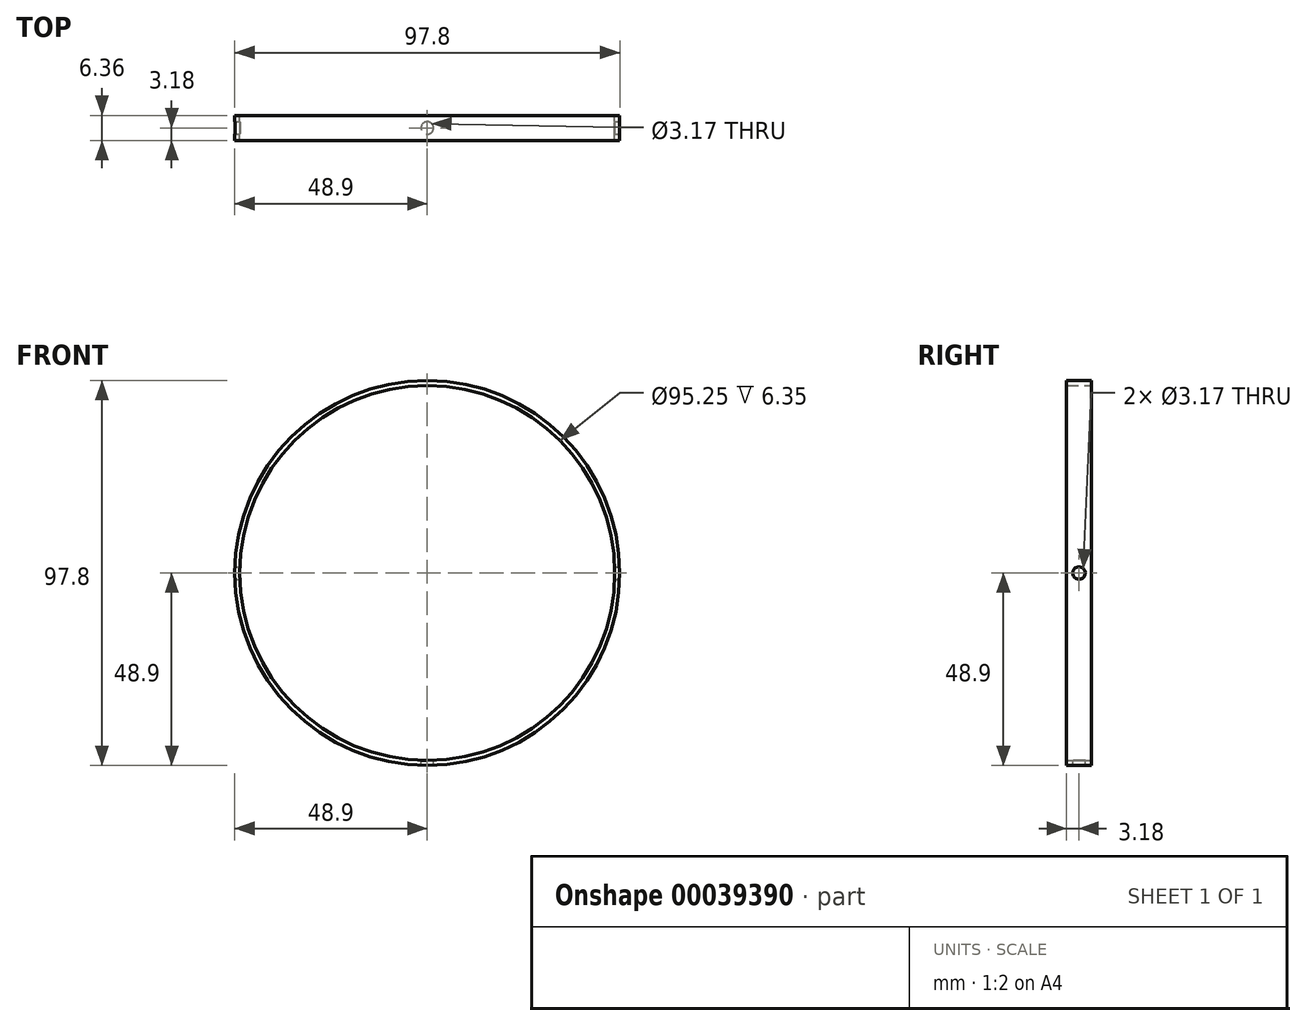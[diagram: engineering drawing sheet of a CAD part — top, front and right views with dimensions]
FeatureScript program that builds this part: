
annotation { "Feature Type Name" : "Feature", "Feature Type Description" : "" }
export const myFeature = defineFeature(function(context is Context, id is Id, definition is map)
    precondition{}
    {
        {
            var Q0;
            Q0=qCreatedBy(makeId("Front.planeOp"),FACE);
            var sketch = newSketch(context, id + "F0", { "sketchPlane" : qUnion([Q0])});
            skCircle(sketch, "E0", {"center": v(0, 0) * mm, "radius": 47.63 * mm});
            skCircle(sketch, "E1", {"center": v(0, 0) * mm, "radius": 48.9 * mm});
            skSolve(sketch);
        }
        {
            var Q0;
            Q0=makeQuery(id+"F0.imprint","IMPRINT",FACE,{"disambiguationData":[TD([[makeQuery(id+"F0.imprint","IMPRINT",EDGE,{"derivedFrom":sQuery(id+"F0.wireOp",EDGE,"E0")}),-1.0]])]});
            extrude(context, id + "F1", {"entities" : qUnion([Q0]), "endBound" : BoundingType.SYMMETRIC, "depth" : 6.35 * mm});
        }
        {
            var Q0;
            Q0=qCreatedBy(makeId("Right.planeOp"),FACE);
            var sketch = newSketch(context, id + "F2", { "sketchPlane" : qUnion([Q0])});
            skCircle(sketch, "E2", {"center": v(0, 0) * mm, "radius": 1.59 * mm});
            skSolve(sketch);
        }
        {
            var Q0;
            Q0 = qSketchRegion(id + "F2", true);
            extrude(context, id + "F3", {"entities" : qUnion([Q0]), "operationType" : NewBodyOperationType.REMOVE, "endBound" : BoundingType.THROUGH_ALL, "oppositeDirection" : true, "depth" : 25.4 * mm, "hasSecondDirection" : true, "secondDirectionOppositeDirection" : false, "secondDirectionDepth" : 88.97 * mm});
        }
        {
            var Q0;
            Q0=qCreatedBy(makeId("Top.planeOp"),FACE);
            var sketch = newSketch(context, id + "F4", { "sketchPlane" : qUnion([Q0])});
            skCircle(sketch, "E3", {"center": v(0, 0) * mm, "radius": 1.59 * mm});
            skSolve(sketch);
        }
        {
            var Q0;
            Q0 = qSketchRegion(id + "F4", true);
            extrude(context, id + "F5", {"entities" : qUnion([Q0]), "operationType" : NewBodyOperationType.REMOVE, "endBound" : BoundingType.THROUGH_ALL, "oppositeDirection" : true, "depth" : 25.4 * mm});
        }
    });
